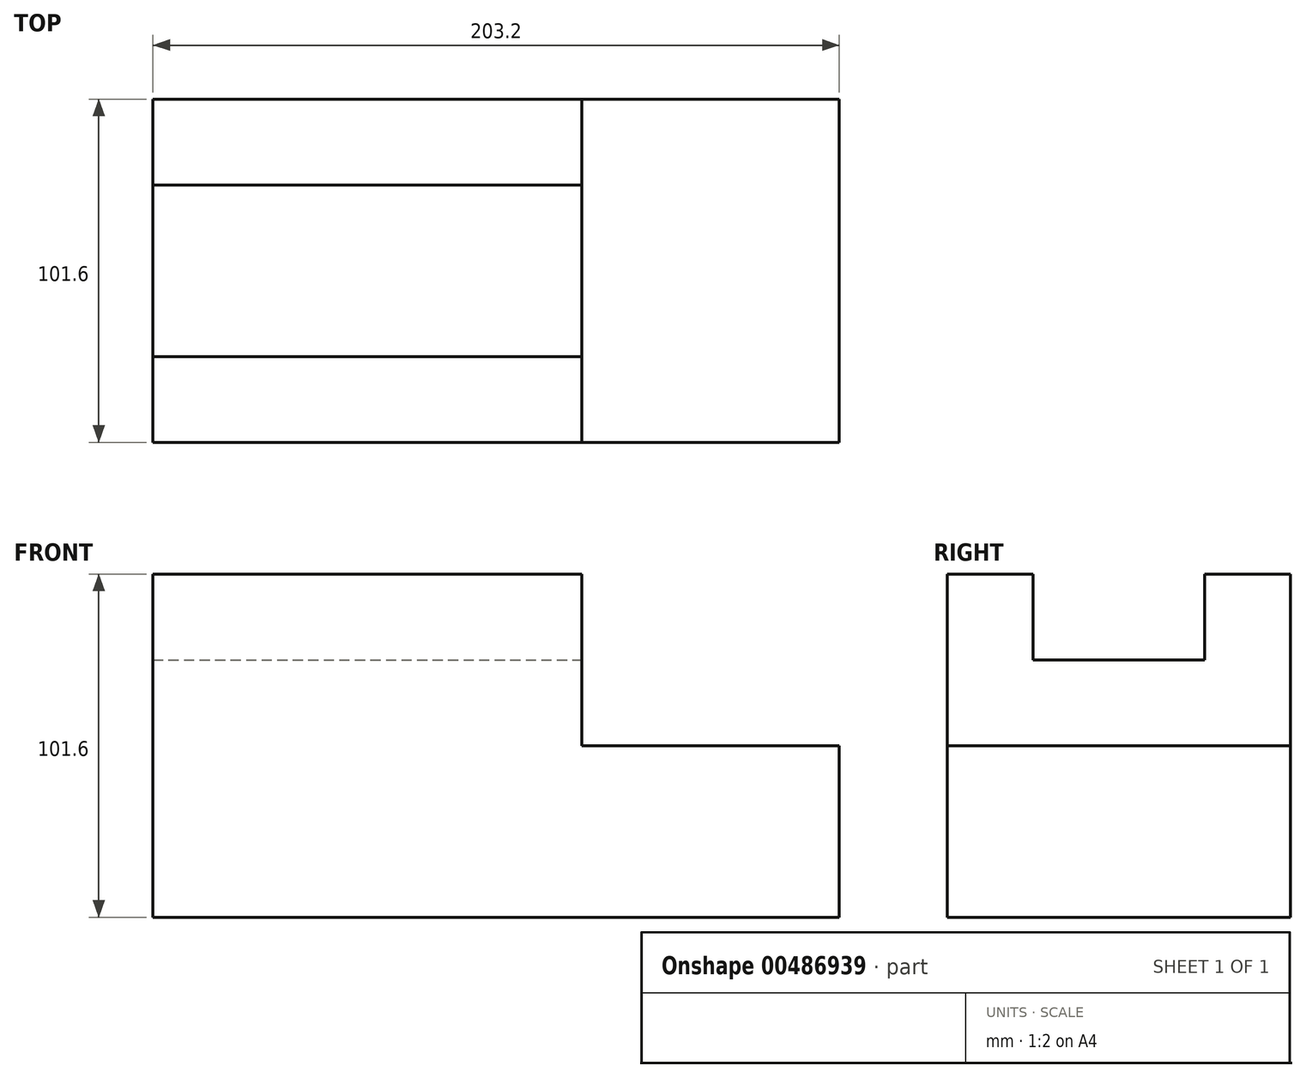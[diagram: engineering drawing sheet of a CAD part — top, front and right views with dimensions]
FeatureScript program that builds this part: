
annotation { "Feature Type Name" : "Feature", "Feature Type Description" : "" }
export const myFeature = defineFeature(function(context is Context, id is Id, definition is map)
    precondition{}
    {
        {
            var Q0;
            Q0=qCreatedBy(makeId("Front.planeOp"),FACE);
            var sketch = newSketch(context, id + "F0", { "sketchPlane" : qUnion([Q0])});
            skLineSegment(sketch, "E0.bottom", {"start": v(-101.6, 50.8) * mm, "end": v(25.4, 50.8) * mm});
            skLineSegment(sketch, "E0.top", {"start": v(-101.6, -50.8) * mm, "end": v(101.6, -50.8) * mm});
            skLineSegment(sketch, "E0.left", {"start": v(-101.6, 50.8) * mm, "end": v(-101.6, -50.8) * mm});
            skLineSegment(sketch, "E0.right", {"start": v(101.6, 0) * mm, "end": v(101.6, -50.8) * mm});
            skPoint(sketch, "E0.middle", {"position": v(0, 0) * mm});
            skLineSegment(sketch, "E1.top", {"start": v(25.4, 0) * mm, "end": v(101.6, 0) * mm});
            skLineSegment(sketch, "E1.left", {"start": v(25.4, 50.8) * mm, "end": v(25.4, 0) * mm});
            skPoint(sketch, "E2.orphan", {"position": v(101.6, 50.8) * mm});
            skSolve(sketch);
        }
        {
            var Q0;
            Q0 = qSketchRegion(id + "F0", true);
            extrude(context, id + "F1", {"entities" : qUnion([Q0]), "depth" : 101.6 * mm});
        }
        {
            var Q0;
            Q0=makeQuery(id+"F1.opExtrude","SWEPT_FACE",FACE,{"disambiguationData":[OSD([sQuery(id+"F0.wireOp",EDGE,"E1.left")])]});
            var sketch = newSketch(context, id + "F2", { "sketchPlane" : qUnion([Q0])});
            skLineSegment(sketch, "E3", {"start": v(-76.2, 50.8) * mm, "end": v(-101.6, 50.8) * mm});
            skLineSegment(sketch, "E4", {"start": v(0, 50.8) * mm, "end": v(-25.4, 50.8) * mm});
            skLineSegment(sketch, "E5.bottom", {"start": v(-76.2, 50.8) * mm, "end": v(-25.4, 50.8) * mm});
            skLineSegment(sketch, "E5.top", {"start": v(-76.2, 25.4) * mm, "end": v(-25.4, 25.4) * mm});
            skLineSegment(sketch, "E5.left", {"start": v(-76.2, 50.8) * mm, "end": v(-76.2, 25.4) * mm});
            skLineSegment(sketch, "E5.right", {"start": v(-25.4, 50.8) * mm, "end": v(-25.4, 25.4) * mm});
            skSolve(sketch);
        }
        {
            var Q0;
            Q0 = qSketchRegion(id + "F2", true);
            extrude(context, id + "F3", {"entities" : qUnion([Q0]), "operationType" : NewBodyOperationType.REMOVE, "oppositeDirection" : true, "depth" : 127 * mm});
        }
    });
